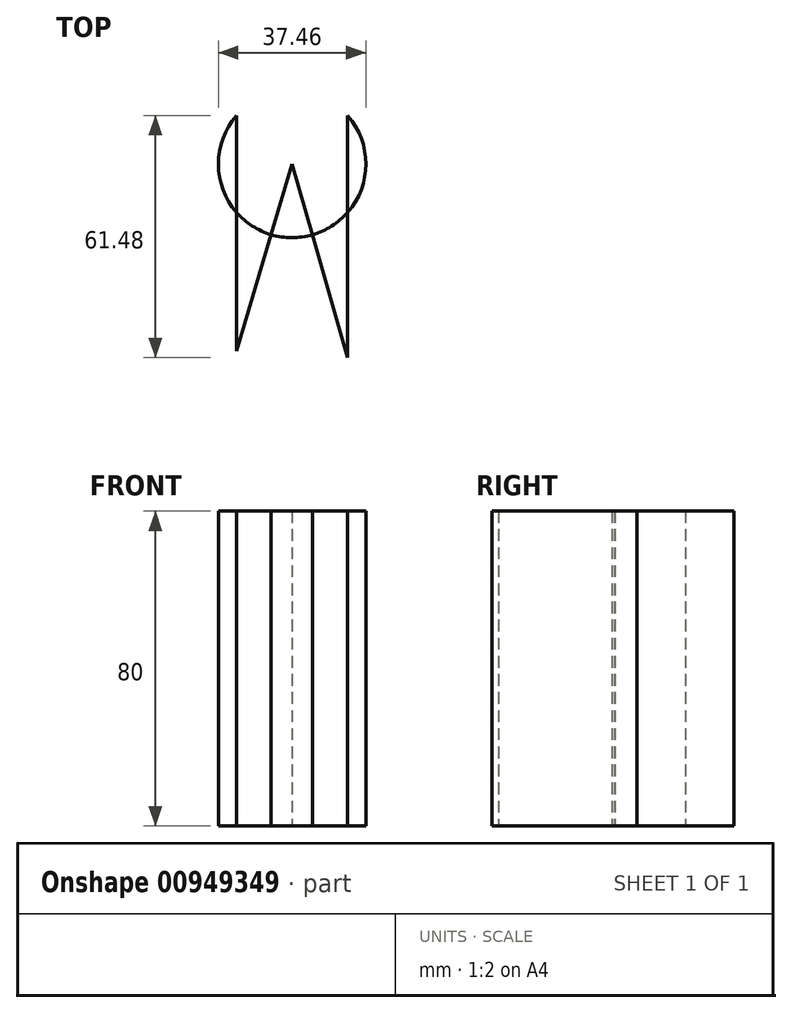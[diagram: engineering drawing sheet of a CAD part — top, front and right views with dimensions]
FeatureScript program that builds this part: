
annotation { "Feature Type Name" : "Feature", "Feature Type Description" : "" }
export const myFeature = defineFeature(function(context is Context, id is Id, definition is map)
    precondition{}
    {
        {
            var Q0;
            Q0=qCreatedBy(makeId("Top.planeOp"),FACE);
            var sketch = newSketch(context, id + "F0", { "sketchPlane" : qUnion([Q0])});
            skLineSegment(sketch, "E0", {"start": v(-28.26, 39.87) * mm, "end": v(-28.26, -19.96) * mm});
            skArc(sketch, "E1", {"start": v(-28.26, 39.87) * mm, "mid": v(-14.13, 8.85) * mm, "end": v(0, 39.87) * mm});
            skLineSegment(sketch, "E2", {"start": v(0, 39.87) * mm, "end": v(0, -21.6) * mm});
            skLineSegment(sketch, "E3", {"start": v(0, -21.6) * mm, "end": v(-14.13, 27.58) * mm});
            skLineSegment(sketch, "E4", {"start": v(-14.13, 27.58) * mm, "end": v(-28.26, -19.96) * mm});
            skSolve(sketch);
        }
        {
            var Q0;
            Q0 = qSketchRegion(id + "F0", true);
            extrude(context, id + "F1", {"entities" : qUnion([Q0]), "endBound" : BoundingType.SYMMETRIC, "depth" : 80 * mm, "offsetDistance" : 25.4 * mm});
        }
    });
